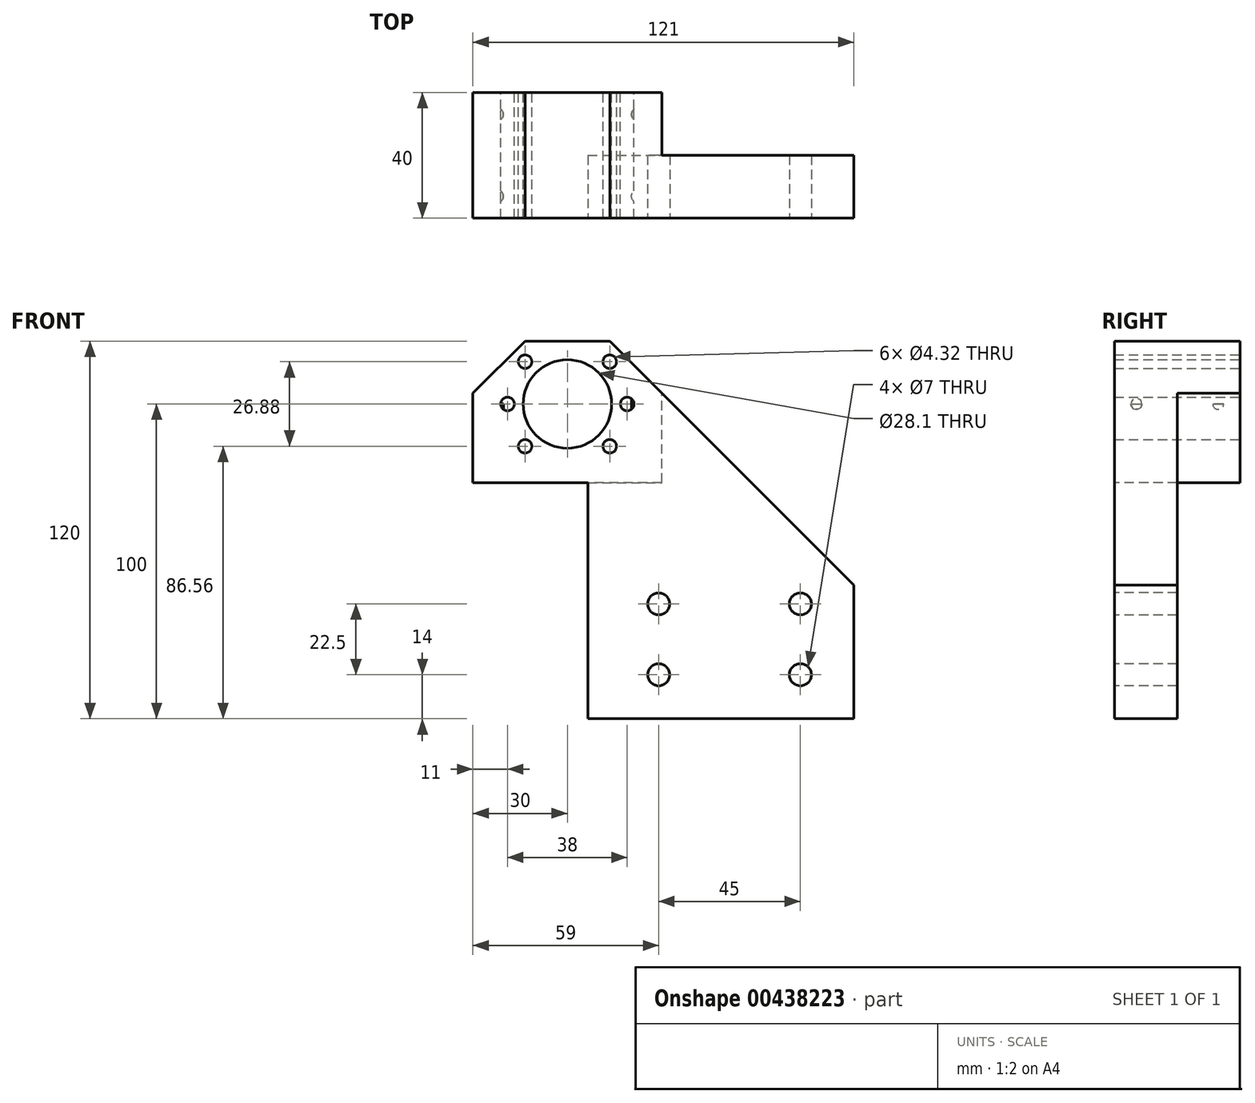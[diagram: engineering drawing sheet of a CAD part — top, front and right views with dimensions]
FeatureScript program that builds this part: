
annotation { "Feature Type Name" : "Feature", "Feature Type Description" : "" }
export const myFeature = defineFeature(function(context is Context, id is Id, definition is map)
    precondition{}
    {
        {
            var Q0;
            Q0=qCreatedBy(makeId("Front.planeOp"),FACE);
            var sketch = newSketch(context, id + "F0", { "sketchPlane" : qUnion([Q0])});
            skLineSegment(sketch, "E0.bottom", {"start": v(30, 22.5) * mm, "end": v(-30, 22.5) * mm});
            skLineSegment(sketch, "E0.top", {"start": v(30, -22.5) * mm, "end": v(-30, -22.5) * mm});
            skLineSegment(sketch, "E0.left", {"start": v(30, 22.5) * mm, "end": v(30, -22.5) * mm});
            skLineSegment(sketch, "E0.right", {"start": v(-30, 22.5) * mm, "end": v(-30, -22.5) * mm});
            skPoint(sketch, "E0.middle", {"position": v(0, 0) * mm});
            skCircle(sketch, "E1", {"center": v(0, -2.5) * mm, "radius": 14.05 * mm});
            skCircle(sketch, "E2", {"center": v(-13.44, -15.94) * mm, "radius": 2.16 * mm});
            skCircle(sketch, "E3", {"center": v(-13.44, 10.94) * mm, "radius": 2.16 * mm});
            skCircle(sketch, "E4", {"center": v(-19, -2.5) * mm, "radius": 2.16 * mm});
            skCircle(sketch, "E5", {"center": v(19, -2.5) * mm, "radius": 2.16 * mm});
            skCircle(sketch, "E6", {"center": v(13.44, 10.94) * mm, "radius": 2.16 * mm});
            skCircle(sketch, "E7", {"center": v(13.44, -15.94) * mm, "radius": 2.16 * mm});
            skLineSegment(sketch, "E8", {"start": v(30, -5.94) * mm, "end": v(13.44, -22.5) * mm, "construction": true});
            skLineSegment(sketch, "E9", {"start": v(-30, -5.94) * mm, "end": v(-13.44, -22.5) * mm, "construction": true});
            skLineSegment(sketch, "E10", {"start": v(-30, -5.94) * mm, "end": v(-13.44, -22.5) * mm});
            skLineSegment(sketch, "E11", {"start": v(30, -5.94) * mm, "end": v(13.44, -22.5) * mm});
            skSolve(sketch);
        }
        {
            var Q0;
            {var subQ0=sQuery(id+"F0.wireOp",EDGE,"E0.bottom");Q0=makeQuery(id+"F0.imprint","IMPRINT",FACE,{"disambiguationData":[TD([[makeQuery(id+"F0.imprint","IMPRINT",EDGE,{"derivedFrom":subQ0}),1.0]])]});}
            extrude(context, id + "F1", {"entities" : qUnion([Q0]), "depth" : 40 * mm});
        }
        {
            var Q0;
            Q0=makeQuery(id+"F1.opExtrude","SWEPT_FACE",FACE,{"disambiguationData":[OSD([sQuery(id+"F0.wireOp",EDGE,"E0.bottom")])]});
            var sketch = newSketch(context, id + "F2", { "sketchPlane" : qUnion([Q0])});
            skCircle(sketch, "E12", {"center": v(-22.5, -33) * mm, "radius": 2.16 * mm});
            skCircle(sketch, "E13", {"center": v(-22.5, -7) * mm, "radius": 2.16 * mm});
            skCircle(sketch, "E14", {"center": v(22.5, -7) * mm, "radius": 2.16 * mm});
            skCircle(sketch, "E15", {"center": v(22.5, -33) * mm, "radius": 2.16 * mm});
            skLineSegment(sketch, "E16", {"start": v(-30, -20) * mm, "end": v(30, -20) * mm, "construction": true});
            skLineSegment(sketch, "E17", {"start": v(0, 0) * mm, "end": v(0, -40) * mm, "construction": true});
            skSolve(sketch);
        }
        {
            var Q0;
            Q0=makeQuery(id+"F2.imprint","IMPRINT",FACE,{"disambiguationData":[TD([[makeQuery(id+"F2.imprint","IMPRINT",EDGE,{"derivedFrom":sQuery(id+"F2.wireOp",EDGE,"E13")}),1.0]])]});
            var Q1;
            Q1=makeQuery(id+"F2.imprint","IMPRINT",FACE,{"disambiguationData":[TD([[makeQuery(id+"F2.imprint","IMPRINT",EDGE,{"derivedFrom":sQuery(id+"F2.wireOp",EDGE,"E14")}),1.0]])]});
            var Q2;
            Q2=makeQuery(id+"F2.imprint","IMPRINT",FACE,{"disambiguationData":[TD([[makeQuery(id+"F2.imprint","IMPRINT",EDGE,{"derivedFrom":sQuery(id+"F2.wireOp",EDGE,"E12")}),1.0]])]});
            var Q3;
            Q3=makeQuery(id+"F2.imprint","IMPRINT",FACE,{"disambiguationData":[TD([[makeQuery(id+"F2.imprint","IMPRINT",EDGE,{"derivedFrom":sQuery(id+"F2.wireOp",EDGE,"E15")}),1.0]])]});
            extrude(context, id + "F3", {"entities" : qUnion([Q0, Q1, Q2, Q3]), "operationType" : NewBodyOperationType.REMOVE, "oppositeDirection" : true, "depth" : 15 * mm});
        }
        {
            var Q0;
            Q0=makeQuery(id+"F2.imprint","IMPRINT",FACE,{"disambiguationData":[TD([[makeQuery(id+"F2.imprint","IMPRINT",EDGE,{"derivedFrom":sQuery(id+"F2.wireOp",EDGE,"E12")}),-1.0]])]});
            var sketch = newSketch(context, id + "F4", { "sketchPlane" : qUnion([Q0])});
            skLineSegment(sketch, "E18", {"start": v(30, 0) * mm, "end": v(30, -40) * mm, "construction": true});
            skLineSegment(sketch, "E19", {"start": v(30, -20) * mm, "end": v(11, -20) * mm, "construction": true});
            skLineSegment(sketch, "E20", {"start": v(11, -20) * mm, "end": v(11, -40) * mm});
            skLineSegment(sketch, "E21", {"start": v(11, -20) * mm, "end": v(30, -20) * mm});
            skSolve(sketch);
        }
        {
            var Q0;
            Q0=makeQuery(id+"F2.imprint","IMPRINT",FACE,{"disambiguationData":[TD([[makeQuery(id+"F2.imprint","IMPRINT",EDGE,{"derivedFrom":sQuery(id+"F2.wireOp",EDGE,"E15")}),1.0]])]});
            var Q1;
            Q1=sQuery(id+"F2.wireOp",EDGE,"E15");
            extrude(context, id + "F5", {"entities" : qUnion([Q0]), "operationType" : NewBodyOperationType.ADD, "surfaceEntities" : qUnion([Q1]), "oppositeDirection" : true, "depth" : 25 * mm});
        }
        {
            var Q0;
            Q0=makeQuery(id+"F2.imprint","IMPRINT",FACE,{"disambiguationData":[TD([[makeQuery(id+"F2.imprint","IMPRINT",EDGE,{"derivedFrom":sQuery(id+"F2.wireOp",EDGE,"E12")}),-1.0]])]});
            var sketch = newSketch(context, id + "F6", { "sketchPlane" : qUnion([Q0])});
            skCircle(sketch, "E22.0", {"center": v(22.5, -7) * mm, "radius": 2.16 * mm});
            skCircle(sketch, "E23.0", {"center": v(22.5, -33) * mm, "radius": 2.16 * mm});
            skCircle(sketch, "E24.0", {"center": v(-22.5, -7) * mm, "radius": 2.16 * mm});
            skCircle(sketch, "E25.0", {"center": v(-22.5, -33) * mm, "radius": 2.16 * mm});
            skSolve(sketch);
        }
        {
            var Q0;
            Q0 = qSketchRegion(id + "F6", true);
            var Q1;
            Q1=makeQuery(id+"F1.opExtrude","SWEPT_FACE",FACE,{"disambiguationData":[OSD([sQuery(id+"F0.wireOp",EDGE,"E11")])]});
            extrude(context, id + "F7", {"entities" : qUnion([Q0]), "operationType" : NewBodyOperationType.ADD, "oppositeDirection" : true, "endBoundEntityFace" : qUnion([Q1]), "depth" : 25 * mm});
        }
        {
            var Q0;
            {var subQ5=sQuery(id+"F4.wireOp",EDGE,"E20");Q0=makeQuery(id+"F4.imprint","IMPRINT",FACE,{"disambiguationData":[TD([[makeQuery(id+"F4.imprint","IMPRINT",EDGE,{"derivedFrom":subQ5}),1.0]])]});}
            extrude(context, id + "F8", {"entities" : qUnion([Q0]), "operationType" : NewBodyOperationType.ADD, "depth" : 25 * mm});
        }
        {
            var Q0;
            Q0=makeQuery(id+"F8.opExtrude","CAP_FACE",FACE,{"disambiguationData":[OSD([sQuery(id+"F0.wireOp",EDGE,"E0.bottom"),sQuery(id+"F0.wireOp",EDGE,"E0.left"),sQuery(id+"F2.wireOp",EDGE,"E15"),sQuery(id+"F4.wireOp",EDGE,"E20"),sQuery(id+"F4.wireOp",EDGE,"E21")])],"isStart":false});
            var sketch = newSketch(context, id + "F9", { "sketchPlane" : qUnion([Q0])});
            skCircle(sketch, "E26.0", {"center": v(22.5, -33) * mm, "radius": 2.16 * mm});
            skLineSegment(sketch, "E27", {"start": v(11, -20) * mm, "end": v(6.5, -20) * mm});
            skLineSegment(sketch, "E28", {"start": v(6.5, -20) * mm, "end": v(6.5, -40) * mm});
            skLineSegment(sketch, "E29", {"start": v(6.5, -40) * mm, "end": v(11, -40) * mm});
            skSolve(sketch);
        }
        {
            var Q0;
            Q0 = qSketchRegion(id + "F9", true);
            extrude(context, id + "F10", {"entities" : qUnion([Q0]), "operationType" : NewBodyOperationType.ADD, "oppositeDirection" : true, "depth" : 57.1 * mm});
        }
        {
            var Q0;
            {var subQ0=sQuery(id+"F0.wireOp",EDGE,"E0.bottom");Q0=makeQuery(id+"F8.boolean.opBoolean","MERGE",FACE,{"derivedFrom":[makeQuery(id+"F1.opExtrude","CAP_FACE",FACE,{"disambiguationData":[OSD([subQ0,sQuery(id+"F0.wireOp",EDGE,"E0.top"),sQuery(id+"F0.wireOp",EDGE,"E0.left"),sQuery(id+"F0.wireOp",EDGE,"E0.right"),sQuery(id+"F0.wireOp",EDGE,"E1"),sQuery(id+"F0.wireOp",EDGE,"E2"),sQuery(id+"F0.wireOp",EDGE,"E3"),sQuery(id+"F0.wireOp",EDGE,"E4"),sQuery(id+"F0.wireOp",EDGE,"E5"),sQuery(id+"F0.wireOp",EDGE,"E6"),sQuery(id+"F0.wireOp",EDGE,"E7"),sQuery(id+"F0.wireOp",EDGE,"E10"),sQuery(id+"F0.wireOp",EDGE,"E11")])],"isStart":false}),makeQuery(id+"F8.opExtrude","SWEPT_FACE",FACE,{"disambiguationData":[OSD([subQ0])]})]});}
            var sketch = newSketch(context, id + "F11", { "sketchPlane" : qUnion([Q0])});
            skLineSegment(sketch, "E30", {"start": v(11, 47.5) * mm, "end": v(11, 97.5) * mm});
            skLineSegment(sketch, "E31", {"start": v(11, 97.5) * mm, "end": v(91, 97.5) * mm});
            skLineSegment(sketch, "E32", {"start": v(30, -5.94) * mm, "end": v(91, 55.06) * mm});
            skLineSegment(sketch, "E33", {"start": v(91, 97.5) * mm, "end": v(91, 55.06) * mm});
            skLineSegment(sketch, "E34", {"start": v(11, 97.5) * mm, "end": v(11, 83.5) * mm});
            skLineSegment(sketch, "E35", {"start": v(11, 83.5) * mm, "end": v(29, 83.5) * mm, "construction": true});
            skLineSegment(sketch, "E36", {"start": v(29, 83.5) * mm, "end": v(74, 83.5) * mm, "construction": true});
            skLineSegment(sketch, "E37", {"start": v(74, 83.5) * mm, "end": v(74, 61) * mm, "construction": true});
            skLineSegment(sketch, "E38", {"start": v(74, 61) * mm, "end": v(29, 61) * mm, "construction": true});
            skCircle(sketch, "E39", {"center": v(29, 83.5) * mm, "radius": 3.5 * mm});
            skCircle(sketch, "E40", {"center": v(74, 83.5) * mm, "radius": 3.5 * mm});
            skCircle(sketch, "E41", {"center": v(74, 61) * mm, "radius": 3.5 * mm});
            skCircle(sketch, "E42", {"center": v(29, 61) * mm, "radius": 3.5 * mm});
            skSolve(sketch);
        }
        {
            var Q0;
            Q0=makeQuery(id+"F11.imprint","IMPRINT",FACE,{"disambiguationData":[TD([[makeQuery(id+"F11.imprint","IMPRINT",EDGE,{"derivedFrom":sQuery(id+"F11.wireOp",EDGE,"E30")}),-1.0]])]});
            var Q1;
            Q1=makeQuery(id+"F8.opExtrude","CAP_VERTEX",VERTEX,{"disambiguationData":[OSD([sQuery(id+"F0.wireOp",EDGE,"E0.bottom"),sQuery(id+"F0.wireOp",EDGE,"E0.left"),sQuery(id+"F4.wireOp",EDGE,"E21")])],"isStart":false});
            extrude(context, id + "F12", {"entities" : qUnion([Q0]), "operationType" : NewBodyOperationType.ADD, "endBound" : BoundingType.UP_TO_VERTEX, "oppositeDirection" : true, "endBoundEntityVertex" : qUnion([Q1]), "depth" : 25 * mm});
        }
        {
            var Q0;
            Q0=makeQuery(id+"F9.imprint","IMPRINT",FACE,{"disambiguationData":[TD([[makeQuery(id+"F9.imprint","IMPRINT",EDGE,{"derivedFrom":sQuery(id+"F9.wireOp",EDGE,"E27")}),1.0]])]});
            extrude(context, id + "F13", {"entities" : qUnion([Q0]), "operationType" : NewBodyOperationType.ADD, "oppositeDirection" : true, "depth" : 25 * mm});
        }
        {
            var Q0;
            Q0=makeQuery(id+"F9.imprint","IMPRINT",FACE,{"disambiguationData":[TD([[makeQuery(id+"F9.imprint","IMPRINT",EDGE,{"derivedFrom":sQuery(id+"F9.wireOp",EDGE,"E27")}),1.0]])]});
            var Q1;
            Q1=makeQuery(id+"F12.opExtrude","CAP_VERTEX",VERTEX,{"disambiguationData":[OSD([sQuery(id+"F11.wireOp",EDGE,"E30"),sQuery(id+"F11.wireOp",EDGE,"E31"),sQuery(id+"F11.wireOp",EDGE,"E34"),dummyQuery(id+"F12.vertexPlane.planeOp",FACE)])],"isStart":false});
            extrude(context, id + "F14", {"entities" : qUnion([Q0]), "operationType" : NewBodyOperationType.ADD, "endBound" : BoundingType.UP_TO_VERTEX, "endBoundEntityVertex" : qUnion([Q1]), "depth" : 25 * mm});
        }
        {
            var Q0;
            Q0=makeQuery(id+"F1.opExtrude","SWEPT_BODY",BODY,{"disambiguationData":[OSD([sQuery(id+"F0.wireOp",EDGE,"E0.bottom"),sQuery(id+"F0.wireOp",EDGE,"E0.top"),sQuery(id+"F0.wireOp",EDGE,"E0.left"),sQuery(id+"F0.wireOp",EDGE,"E0.right"),sQuery(id+"F0.wireOp",EDGE,"E1"),sQuery(id+"F0.wireOp",EDGE,"E2"),sQuery(id+"F0.wireOp",EDGE,"E3"),sQuery(id+"F0.wireOp",EDGE,"E4"),sQuery(id+"F0.wireOp",EDGE,"E5"),sQuery(id+"F0.wireOp",EDGE,"E6"),sQuery(id+"F0.wireOp",EDGE,"E7"),sQuery(id+"F0.wireOp",EDGE,"E10"),sQuery(id+"F0.wireOp",EDGE,"E11")])]});
            var Q1;
            Q1=qCreatedBy(makeId("Top.planeOp"),FACE);
            mirror(context, id + "F15", {"entities" : qUnion([Q0]), "mirrorPlane" : qUnion([Q1])});
        }
        {
            var Q0;
            Q0=makeQuery(id+"F1.opExtrude","SWEPT_BODY",BODY,{"disambiguationData":[OSD([sQuery(id+"F0.wireOp",EDGE,"E0.bottom"),sQuery(id+"F0.wireOp",EDGE,"E0.top"),sQuery(id+"F0.wireOp",EDGE,"E0.left"),sQuery(id+"F0.wireOp",EDGE,"E0.right"),sQuery(id+"F0.wireOp",EDGE,"E1"),sQuery(id+"F0.wireOp",EDGE,"E2"),sQuery(id+"F0.wireOp",EDGE,"E3"),sQuery(id+"F0.wireOp",EDGE,"E4"),sQuery(id+"F0.wireOp",EDGE,"E5"),sQuery(id+"F0.wireOp",EDGE,"E6"),sQuery(id+"F0.wireOp",EDGE,"E7"),sQuery(id+"F0.wireOp",EDGE,"E10"),sQuery(id+"F0.wireOp",EDGE,"E11")])]});
            deleteBodies(context, id + "F16", {"entities" : qUnion([Q0])});
        }
    });
